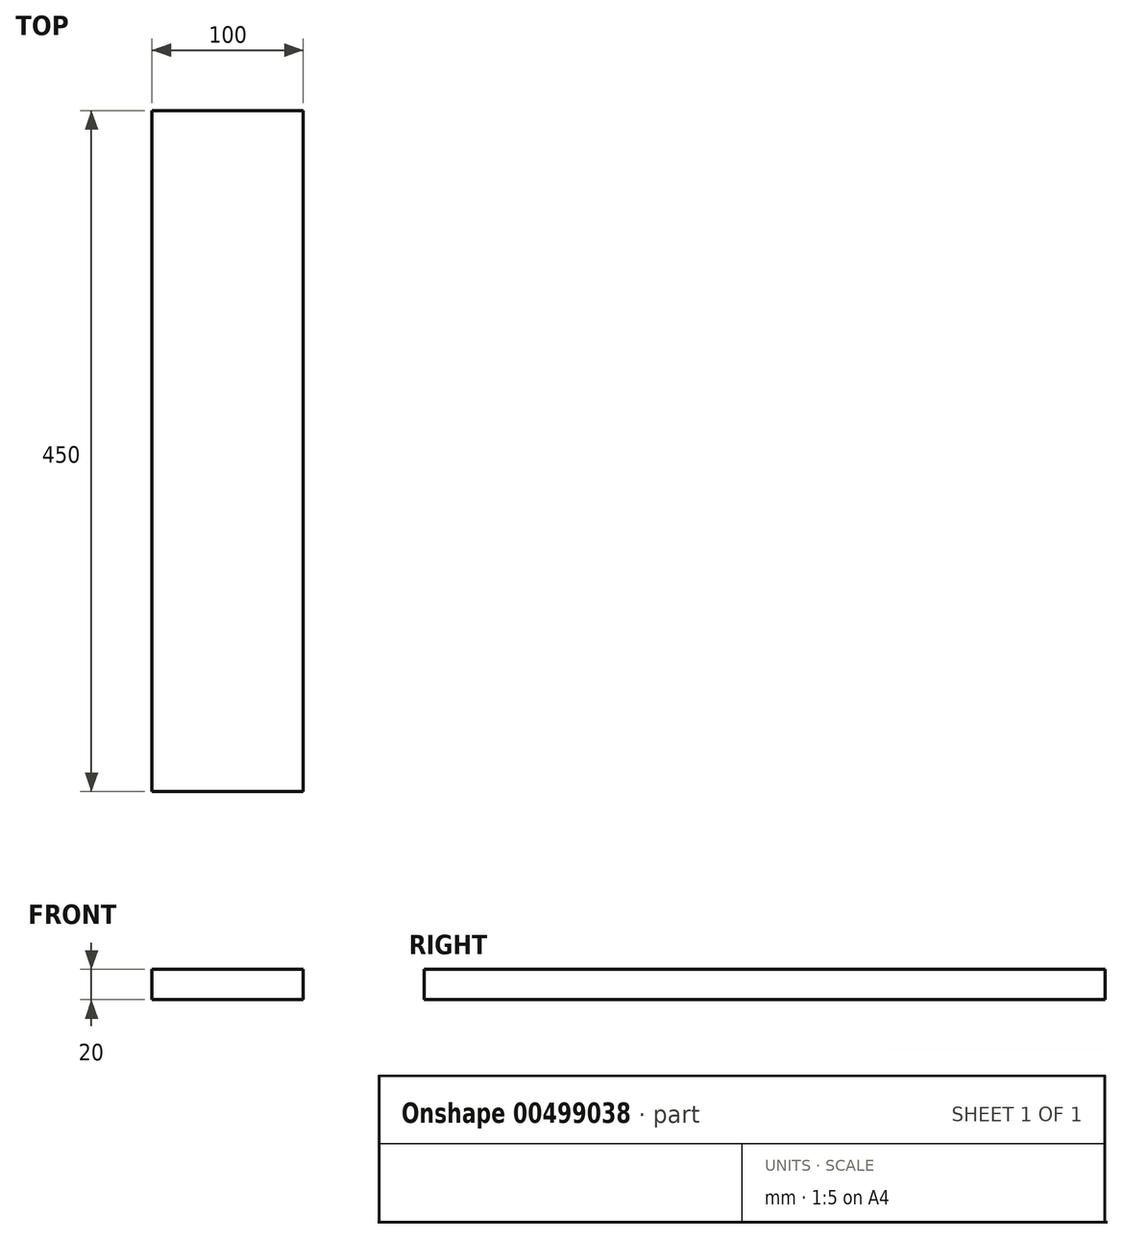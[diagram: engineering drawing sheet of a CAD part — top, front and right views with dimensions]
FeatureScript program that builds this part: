
annotation { "Feature Type Name" : "Feature", "Feature Type Description" : "" }
export const myFeature = defineFeature(function(context is Context, id is Id, definition is map)
    precondition{}
    {
        {
            var Q0;
            Q0=qCreatedBy(makeId("Top.planeOp"),FACE);
            var sketch = newSketch(context, id + "F0", { "sketchPlane" : qUnion([Q0])});
            skLineSegment(sketch, "E0.bottom", {"start": v(-90.44, 310.58) * mm, "end": v(9.56, 310.58) * mm});
            skLineSegment(sketch, "E0.top", {"start": v(-90.44, -139.42) * mm, "end": v(9.56, -139.42) * mm});
            skLineSegment(sketch, "E0.left", {"start": v(-90.44, 310.58) * mm, "end": v(-90.44, -139.42) * mm});
            skLineSegment(sketch, "E0.right", {"start": v(9.56, 310.58) * mm, "end": v(9.56, -139.42) * mm});
            skSolve(sketch);
        }
        {
            var Q0;
            Q0 = qSketchRegion(id + "F0", true);
            extrude(context, id + "F1", {"entities" : qUnion([Q0]), "depth" : 20 * mm, "offsetDistance" : 25 * mm});
        }
    });
